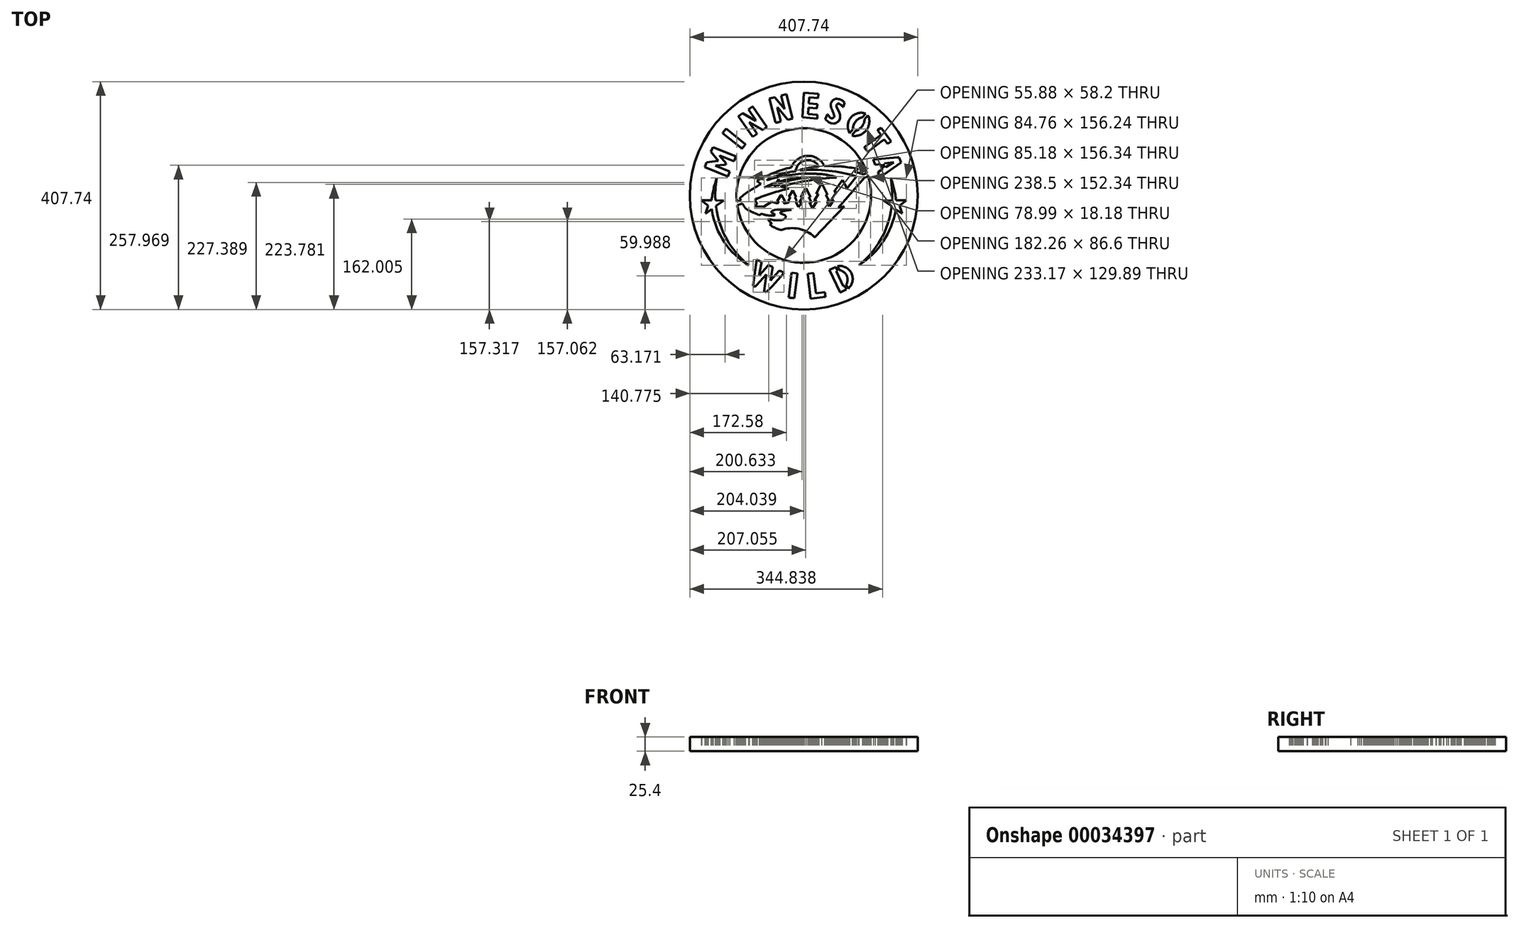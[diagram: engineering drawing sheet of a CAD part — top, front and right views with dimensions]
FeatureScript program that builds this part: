
annotation { "Feature Type Name" : "Feature", "Feature Type Description" : "" }
export const myFeature = defineFeature(function(context is Context, id is Id, definition is map)
    precondition{}
    {
        {
            var Q0;
            Q0=qCreatedBy(makeId("Top.planeOp"),FACE);
            var sketch = newSketch(context, id + "F0", { "sketchPlane" : qUnion([Q0])});
            skLineSegment(sketch, "E0", {"start": v(13.66, -184.3) * mm, "end": v(38.88, -181.07) * mm});
            skLineSegment(sketch, "E1", {"start": v(38.88, -181.07) * mm, "end": v(38.67, -180.35) * mm});
            skLineSegment(sketch, "E2", {"start": v(38.67, -180.35) * mm, "end": v(38.62, -180.14) * mm});
            skLineSegment(sketch, "E3", {"start": v(38.62, -180.14) * mm, "end": v(38.56, -179.8) * mm});
            skLineSegment(sketch, "E4", {"start": v(38.56, -179.8) * mm, "end": v(38.43, -178.87) * mm});
            skLineSegment(sketch, "E5", {"start": v(38.43, -178.87) * mm, "end": v(38.28, -177.67) * mm});
            skLineSegment(sketch, "E6", {"start": v(38.28, -177.67) * mm, "end": v(38.15, -176.34) * mm});
            skLineSegment(sketch, "E7", {"start": v(38.15, -176.34) * mm, "end": v(37.84, -173.04) * mm});
            skLineSegment(sketch, "E8", {"start": v(37.84, -173.04) * mm, "end": v(36.9, -173.04) * mm});
            skLineSegment(sketch, "E9", {"start": v(36.9, -173.04) * mm, "end": v(21.99, -174.94) * mm});
            skLineSegment(sketch, "E10", {"start": v(21.99, -174.94) * mm, "end": v(21.52, -174.47) * mm});
            skLineSegment(sketch, "E11", {"start": v(21.52, -174.47) * mm, "end": v(16.96, -139.2) * mm});
            skLineSegment(sketch, "E12", {"start": v(16.96, -139.2) * mm, "end": v(16.62, -138.84) * mm});
            skLineSegment(sketch, "E13", {"start": v(16.62, -138.84) * mm, "end": v(7.3, -139.96) * mm});
            skLineSegment(sketch, "E14", {"start": v(7.3, -139.96) * mm, "end": v(6.76, -140.57) * mm});
            skLineSegment(sketch, "E15", {"start": v(6.76, -140.57) * mm, "end": v(12.46, -184.17) * mm});
            skLineSegment(sketch, "E16", {"start": v(12.46, -184.17) * mm, "end": v(12.49, -184.28) * mm});
            skLineSegment(sketch, "E17", {"start": v(12.49, -184.28) * mm, "end": v(12.5, -184.3) * mm});
            skLineSegment(sketch, "E18", {"start": v(12.5, -184.3) * mm, "end": v(12.55, -184.32) * mm});
            skLineSegment(sketch, "E19", {"start": v(12.55, -184.32) * mm, "end": v(12.68, -184.35) * mm});
            skLineSegment(sketch, "E20", {"start": v(12.68, -184.35) * mm, "end": v(12.87, -184.36) * mm});
            skLineSegment(sketch, "E21", {"start": v(12.87, -184.36) * mm, "end": v(13.09, -184.34) * mm});
            skLineSegment(sketch, "E22", {"start": v(13.09, -184.34) * mm, "end": v(13.66, -184.3) * mm});
            skLineSegment(sketch, "E23", {"start": v(-16.77, -183.6) * mm, "end": v(-11.59, -139.7) * mm});
            skLineSegment(sketch, "E24", {"start": v(-11.59, -139.7) * mm, "end": v(-11.9, -139.4) * mm});
            skLineSegment(sketch, "E25", {"start": v(-11.9, -139.4) * mm, "end": v(-21.63, -138.21) * mm});
            skLineSegment(sketch, "E26", {"start": v(-21.63, -138.21) * mm, "end": v(-21.92, -139.2) * mm});
            skLineSegment(sketch, "E27", {"start": v(-21.92, -139.2) * mm, "end": v(-26.6, -179.63) * mm});
            skLineSegment(sketch, "E28", {"start": v(-26.6, -179.63) * mm, "end": v(-27.07, -182.45) * mm});
            skLineSegment(sketch, "E29", {"start": v(-27.07, -182.45) * mm, "end": v(-25.33, -182.72) * mm});
            skLineSegment(sketch, "E30", {"start": v(-25.33, -182.72) * mm, "end": v(-24.38, -182.85) * mm});
            skLineSegment(sketch, "E31", {"start": v(-24.38, -182.85) * mm, "end": v(-23.1, -183) * mm});
            skLineSegment(sketch, "E32", {"start": v(-23.1, -183) * mm, "end": v(-21.64, -183.16) * mm});
            skLineSegment(sketch, "E33", {"start": v(-21.64, -183.16) * mm, "end": v(-20.18, -183.3) * mm});
            skLineSegment(sketch, "E34", {"start": v(-20.18, -183.3) * mm, "end": v(-16.77, -183.6) * mm});
            skLineSegment(sketch, "E35", {"start": v(65, -173.44) * mm, "end": v(76.13, -168.01) * mm});
            skLineSegment(sketch, "E36", {"start": v(56.92, -127.66) * mm, "end": v(45.73, -133) * mm});
            skLineSegment(sketch, "E37", {"start": v(45.73, -133) * mm, "end": v(64.83, -173.27) * mm});
            skLineSegment(sketch, "E38", {"start": v(64.83, -173.27) * mm, "end": v(65, -173.44) * mm});
            skLineSegment(sketch, "E39", {"start": v(-67, -172.98) * mm, "end": v(-56.7, -161.92) * mm});
            skLineSegment(sketch, "E40", {"start": v(-56.7, -161.92) * mm, "end": v(-35.8, -139.2) * mm});
            skLineSegment(sketch, "E41", {"start": v(-35.8, -139.2) * mm, "end": v(-35.15, -138.14) * mm});
            skLineSegment(sketch, "E42", {"start": v(-35.15, -138.14) * mm, "end": v(-43.96, -133.96) * mm});
            skLineSegment(sketch, "E43", {"start": v(-43.96, -133.96) * mm, "end": v(-44.55, -134.67) * mm});
            skLineSegment(sketch, "E44", {"start": v(-44.55, -134.67) * mm, "end": v(-59.36, -152.18) * mm});
            skLineSegment(sketch, "E45", {"start": v(-59.36, -152.18) * mm, "end": v(-59.73, -151.81) * mm});
            skLineSegment(sketch, "E46", {"start": v(-59.73, -151.81) * mm, "end": v(-56.06, -128.63) * mm});
            skLineSegment(sketch, "E47", {"start": v(-56.06, -128.63) * mm, "end": v(-56.06, -128.06) * mm});
            skLineSegment(sketch, "E48", {"start": v(-56.06, -128.06) * mm, "end": v(-63.05, -124.87) * mm});
            skLineSegment(sketch, "E49", {"start": v(-63.05, -124.87) * mm, "end": v(-64, -125.24) * mm});
            skLineSegment(sketch, "E50", {"start": v(-64, -125.24) * mm, "end": v(-79.45, -142.55) * mm});
            skLineSegment(sketch, "E51", {"start": v(-79.45, -142.55) * mm, "end": v(-79.98, -142.61) * mm});
            skLineSegment(sketch, "E52", {"start": v(-79.98, -142.61) * mm, "end": v(-76.14, -121.95) * mm});
            skLineSegment(sketch, "E53", {"start": v(-76.14, -121.95) * mm, "end": v(-75.54, -118.77) * mm});
            skLineSegment(sketch, "E54", {"start": v(-75.54, -118.77) * mm, "end": v(-84.25, -114.78) * mm});
            skLineSegment(sketch, "E55", {"start": v(-84.25, -114.78) * mm, "end": v(-84.6, -115.14) * mm});
            skLineSegment(sketch, "E56", {"start": v(-84.6, -115.14) * mm, "end": v(-91.04, -160.1) * mm});
            skLineSegment(sketch, "E57", {"start": v(-91.04, -160.1) * mm, "end": v(-91.03, -161.67) * mm});
            skLineSegment(sketch, "E58", {"start": v(-91.03, -161.67) * mm, "end": v(-87.32, -163.57) * mm});
            skLineSegment(sketch, "E59", {"start": v(-87.32, -163.57) * mm, "end": v(-84.45, -160.3) * mm});
            skLineSegment(sketch, "E60", {"start": v(-84.45, -160.3) * mm, "end": v(-67.19, -141.39) * mm});
            skLineSegment(sketch, "E61", {"start": v(-67.19, -141.39) * mm, "end": v(-66.94, -142.84) * mm});
            skLineSegment(sketch, "E62", {"start": v(-66.94, -142.84) * mm, "end": v(-71, -170.98) * mm});
            skLineSegment(sketch, "E63", {"start": v(-71, -170.98) * mm, "end": v(-70.8, -171.17) * mm});
            skLineSegment(sketch, "E64", {"start": v(-70.8, -171.17) * mm, "end": v(-70.72, -171.23) * mm});
            skLineSegment(sketch, "E65", {"start": v(-70.72, -171.23) * mm, "end": v(-70.58, -171.31) * mm});
            skLineSegment(sketch, "E66", {"start": v(-70.58, -171.31) * mm, "end": v(-70.13, -171.55) * mm});
            skLineSegment(sketch, "E67", {"start": v(-70.13, -171.55) * mm, "end": v(-69.52, -171.85) * mm});
            skLineSegment(sketch, "E68", {"start": v(-69.52, -171.85) * mm, "end": v(-68.8, -172.18) * mm});
            skLineSegment(sketch, "E69", {"start": v(-68.8, -172.18) * mm, "end": v(-67, -172.98) * mm});
            skLineSegment(sketch, "E70", {"start": v(58.62, -136.07) * mm, "end": v(70.8, -162.14) * mm});
            skLineSegment(sketch, "E71", {"start": v(70.8, -162.14) * mm, "end": v(71, -162.14) * mm});
            skLineSegment(sketch, "E72", {"start": v(71, -162.14) * mm, "end": v(71.1, -162.12) * mm});
            skLineSegment(sketch, "E73", {"start": v(71.1, -162.12) * mm, "end": v(71.26, -162.05) * mm});
            skLineSegment(sketch, "E74", {"start": v(71.26, -162.05) * mm, "end": v(71.81, -161.78) * mm});
            skLineSegment(sketch, "E75", {"start": v(71.81, -161.78) * mm, "end": v(72.58, -161.4) * mm});
            skLineSegment(sketch, "E76", {"start": v(72.58, -161.4) * mm, "end": v(72.9, -161.22) * mm});
            skLineSegment(sketch, "E77", {"start": v(60.23, -134.6) * mm, "end": v(58.62, -135.24) * mm});
            skLineSegment(sketch, "E78", {"start": v(58.62, -135.24) * mm, "end": v(58.62, -136.07) * mm});
            skLineSegment(sketch, "E79", {"start": v(-157, -20.94) * mm, "end": v(-157.12, -18.94) * mm});
            skLineSegment(sketch, "E80", {"start": v(-157.12, -18.94) * mm, "end": v(-143.14, -8.86) * mm});
            skLineSegment(sketch, "E81", {"start": v(-143.14, -8.86) * mm, "end": v(-158.2, -8.6) * mm});
            skLineSegment(sketch, "E82", {"start": v(-165.07, -8.63) * mm, "end": v(-183.29, -8.63) * mm});
            skLineSegment(sketch, "E83", {"start": v(-183.29, -8.63) * mm, "end": v(-182.8, -9.43) * mm});
            skLineSegment(sketch, "E84", {"start": v(-182.8, -9.43) * mm, "end": v(-171.8, -17.37) * mm});
            skLineSegment(sketch, "E85", {"start": v(-171.8, -17.37) * mm, "end": v(-171.34, -18.6) * mm});
            skLineSegment(sketch, "E86", {"start": v(-171.34, -18.6) * mm, "end": v(-175.9, -32.25) * mm});
            skLineSegment(sketch, "E87", {"start": v(-175.9, -32.25) * mm, "end": v(-175.28, -32.2) * mm});
            skLineSegment(sketch, "E88", {"start": v(-175.28, -32.2) * mm, "end": v(-164.84, -24.62) * mm});
            skLineSegment(sketch, "E89", {"start": v(-164.84, -24.62) * mm, "end": v(-164.5, -24.83) * mm});
            skLineSegment(sketch, "E90", {"start": v(-164.5, -24.83) * mm, "end": v(-164.43, -24.89) * mm});
            skLineSegment(sketch, "E91", {"start": v(-164.43, -24.89) * mm, "end": v(-164.36, -24.99) * mm});
            skLineSegment(sketch, "E92", {"start": v(-164.36, -24.99) * mm, "end": v(-164.3, -25.11) * mm});
            skLineSegment(sketch, "E93", {"start": v(-164.3, -25.11) * mm, "end": v(-164.26, -25.26) * mm});
            skLineSegment(sketch, "E94", {"start": v(-164.26, -25.26) * mm, "end": v(-164.21, -25.44) * mm});
            skLineSegment(sketch, "E95", {"start": v(-164.21, -25.44) * mm, "end": v(-164.18, -25.63) * mm});
            skLineSegment(sketch, "E96", {"start": v(-164.18, -25.63) * mm, "end": v(-164.16, -25.82) * mm});
            skLineSegment(sketch, "E97", {"start": v(-164.16, -25.82) * mm, "end": v(-164.15, -26.03) * mm});
            skLineSegment(sketch, "E98", {"start": v(-164.15, -26.03) * mm, "end": v(-164.15, -27.02) * mm});
            skLineSegment(sketch, "E99", {"start": v(164.67, -24.98) * mm, "end": v(165.13, -24.98) * mm});
            skLineSegment(sketch, "E100", {"start": v(165.13, -24.98) * mm, "end": v(175.51, -32.25) * mm});
            skLineSegment(sketch, "E101", {"start": v(175.51, -32.25) * mm, "end": v(175.96, -32.25) * mm});
            skLineSegment(sketch, "E102", {"start": v(175.96, -32.25) * mm, "end": v(171.4, -18.6) * mm});
            skLineSegment(sketch, "E103", {"start": v(171.4, -18.6) * mm, "end": v(171.87, -17.37) * mm});
            skLineSegment(sketch, "E104", {"start": v(171.87, -17.37) * mm, "end": v(182.85, -9.43) * mm});
            skLineSegment(sketch, "E105", {"start": v(182.85, -9.43) * mm, "end": v(183.35, -8.63) * mm});
            skLineSegment(sketch, "E106", {"start": v(183.35, -8.63) * mm, "end": v(165.17, -8.63) * mm});
            skLineSegment(sketch, "E107", {"start": v(158.25, -8.6) * mm, "end": v(143.2, -8.86) * mm});
            skLineSegment(sketch, "E108", {"start": v(143.2, -8.86) * mm, "end": v(157.18, -18.94) * mm});
            skLineSegment(sketch, "E109", {"start": v(157.18, -18.94) * mm, "end": v(157.06, -20.94) * mm});
            skLineSegment(sketch, "E110", {"start": v(19.39, -74.33) * mm, "end": v(19.67, -74.26) * mm});
            skLineSegment(sketch, "E111", {"start": v(19.67, -74.26) * mm, "end": v(72.6, -19.3) * mm});
            skLineSegment(sketch, "E112", {"start": v(72.6, -19.3) * mm, "end": v(61.4, -21.73) * mm});
            skLineSegment(sketch, "E113", {"start": v(61.4, -21.73) * mm, "end": v(108.8, 32.15) * mm});
            skLineSegment(sketch, "E114", {"start": v(90.99, 42.52) * mm, "end": v(97.42, 47.42) * mm});
            skLineSegment(sketch, "E115", {"start": v(97.42, 47.42) * mm, "end": v(97.18, 47.66) * mm});
            skLineSegment(sketch, "E116", {"start": v(-83.9, 25.97) * mm, "end": v(-76.46, 20.53) * mm});
            skLineSegment(sketch, "E117", {"start": v(-100.7, -25.36) * mm, "end": v(-95.75, -27.84) * mm});
            skLineSegment(sketch, "E118", {"start": v(-82.13, -34) * mm, "end": v(-79.8, -34.9) * mm});
            skLineSegment(sketch, "E119", {"start": v(-79.8, -34.9) * mm, "end": v(-75.2, -32.78) * mm});
            skLineSegment(sketch, "E120", {"start": v(-75.2, -32.78) * mm, "end": v(-71.8, -33.86) * mm});
            skLineSegment(sketch, "E121", {"start": v(-65.51, -35.4) * mm, "end": v(-62.65, -35.87) * mm});
            skLineSegment(sketch, "E122", {"start": v(-62.65, -35.87) * mm, "end": v(-53.83, -35.88) * mm});
            skLineSegment(sketch, "E123", {"start": v(-53.83, -35.88) * mm, "end": v(-51.5, -34.82) * mm});
            skLineSegment(sketch, "E124", {"start": v(-51.5, -34.82) * mm, "end": v(-51.65, -34.33) * mm});
            skLineSegment(sketch, "E125", {"start": v(-54.73, -32.24) * mm, "end": v(-57.64, -30.65) * mm});
            skLineSegment(sketch, "E126", {"start": v(-56.42, -27.3) * mm, "end": v(-52.2, -25.85) * mm});
            skLineSegment(sketch, "E127", {"start": v(-52.2, -25.85) * mm, "end": v(-42.04, -24.87) * mm});
            skLineSegment(sketch, "E128", {"start": v(-42.04, -24.87) * mm, "end": v(-22.22, -25.6) * mm});
            skLineSegment(sketch, "E129", {"start": v(-38.74, -28.2) * mm, "end": v(-41.75, -30.24) * mm});
            skLineSegment(sketch, "E130", {"start": v(-41.75, -30.24) * mm, "end": v(-41.75, -31.97) * mm});
            skLineSegment(sketch, "E131", {"start": v(-41.75, -31.97) * mm, "end": v(-33.72, -35.39) * mm});
            skLineSegment(sketch, "E132", {"start": v(-32.44, -38.94) * mm, "end": v(-34.35, -41.36) * mm});
            skLineSegment(sketch, "E133", {"start": v(-43.12, -44.24) * mm, "end": v(-53.56, -44.28) * mm});
            skLineSegment(sketch, "E134", {"start": v(-53.56, -44.28) * mm, "end": v(-62.37, -42.12) * mm});
            skLineSegment(sketch, "E135", {"start": v(-62.37, -42.12) * mm, "end": v(-63.81, -42.68) * mm});
            skLineSegment(sketch, "E136", {"start": v(-63.81, -42.68) * mm, "end": v(-62.45, -45.31) * mm});
            skLineSegment(sketch, "E137", {"start": v(-62.45, -45.31) * mm, "end": v(-60.33, -47.18) * mm});
            skLineSegment(sketch, "E138", {"start": v(-57.79, -49.05) * mm, "end": v(-57.37, -49.05) * mm});
            skLineSegment(sketch, "E139", {"start": v(-57.37, -49.05) * mm, "end": v(-57.65, -49.5) * mm});
            skLineSegment(sketch, "E140", {"start": v(-59.53, -50.79) * mm, "end": v(-61.13, -51.6) * mm});
            skLineSegment(sketch, "E141", {"start": v(-61.13, -51.6) * mm, "end": v(-57.28, -55.08) * mm});
            skLineSegment(sketch, "E142", {"start": v(23.78, -9.76) * mm, "end": v(19.33, -9.49) * mm});
            skLineSegment(sketch, "E143", {"start": v(19.33, -9.49) * mm, "end": v(19.33, -8.67) * mm});
            skLineSegment(sketch, "E144", {"start": v(19.33, -8.67) * mm, "end": v(25.8, 1.58) * mm});
            skLineSegment(sketch, "E145", {"start": v(25.8, 1.58) * mm, "end": v(26.24, 2.73) * mm});
            skLineSegment(sketch, "E146", {"start": v(26.24, 2.73) * mm, "end": v(24.15, 2.73) * mm});
            skLineSegment(sketch, "E147", {"start": v(24.15, 2.73) * mm, "end": v(23.34, 2.74) * mm});
            skLineSegment(sketch, "E148", {"start": v(23.34, 2.74) * mm, "end": v(22.67, 2.78) * mm});
            skLineSegment(sketch, "E149", {"start": v(22.67, 2.78) * mm, "end": v(22.42, 2.8) * mm});
            skLineSegment(sketch, "E150", {"start": v(22.42, 2.8) * mm, "end": v(22.22, 2.83) * mm});
            skLineSegment(sketch, "E151", {"start": v(22.22, 2.83) * mm, "end": v(22.1, 2.86) * mm});
            skLineSegment(sketch, "E152", {"start": v(22.1, 2.86) * mm, "end": v(22.07, 2.88) * mm});
            skLineSegment(sketch, "E153", {"start": v(22.07, 2.88) * mm, "end": v(22.06, 2.9) * mm});
            skLineSegment(sketch, "E154", {"start": v(22.06, 2.9) * mm, "end": v(22.06, 3.06) * mm});
            skLineSegment(sketch, "E155", {"start": v(22.06, 3.06) * mm, "end": v(32.04, 22.88) * mm});
            skLineSegment(sketch, "E156", {"start": v(32.04, 22.88) * mm, "end": v(42.04, 2.22) * mm});
            skLineSegment(sketch, "E157", {"start": v(42.04, 2.22) * mm, "end": v(42.04, 1.42) * mm});
            skLineSegment(sketch, "E158", {"start": v(42.04, 1.42) * mm, "end": v(39.3, 1.14) * mm});
            skLineSegment(sketch, "E159", {"start": v(39.3, 1.14) * mm, "end": v(45.22, -9.08) * mm});
            skLineSegment(sketch, "E160", {"start": v(45.22, -9.08) * mm, "end": v(45.22, -9.3) * mm});
            skLineSegment(sketch, "E161", {"start": v(45.22, -9.3) * mm, "end": v(45.21, -9.33) * mm});
            skLineSegment(sketch, "E162", {"start": v(45.21, -9.33) * mm, "end": v(45.18, -9.35) * mm});
            skLineSegment(sketch, "E163", {"start": v(45.18, -9.35) * mm, "end": v(45.06, -9.4) * mm});
            skLineSegment(sketch, "E164", {"start": v(45.06, -9.4) * mm, "end": v(44.87, -9.44) * mm});
            skLineSegment(sketch, "E165", {"start": v(44.87, -9.44) * mm, "end": v(44.62, -9.47) * mm});
            skLineSegment(sketch, "E166", {"start": v(44.62, -9.47) * mm, "end": v(44.32, -9.5) * mm});
            skLineSegment(sketch, "E167", {"start": v(44.32, -9.5) * mm, "end": v(43.97, -9.52) * mm});
            skLineSegment(sketch, "E168", {"start": v(43.97, -9.52) * mm, "end": v(43.58, -9.53) * mm});
            skLineSegment(sketch, "E169", {"start": v(43.58, -9.53) * mm, "end": v(43.17, -9.54) * mm});
            skLineSegment(sketch, "E170", {"start": v(43.17, -9.54) * mm, "end": v(41.12, -9.54) * mm});
            skLineSegment(sketch, "E171", {"start": v(41.12, -9.54) * mm, "end": v(41.76, -11.01) * mm});
            skLineSegment(sketch, "E172", {"start": v(41.76, -11.01) * mm, "end": v(42.14, -11.87) * mm});
            skLineSegment(sketch, "E173", {"start": v(42.14, -11.87) * mm, "end": v(42.7, -13.1) * mm});
            skLineSegment(sketch, "E174", {"start": v(42.7, -13.1) * mm, "end": v(44.08, -16.05) * mm});
            skLineSegment(sketch, "E175", {"start": v(44.08, -16.05) * mm, "end": v(45.77, -19.62) * mm});
            skLineSegment(sketch, "E176", {"start": v(45.77, -19.62) * mm, "end": v(46.45, -18.85) * mm});
            skLineSegment(sketch, "E177", {"start": v(46.45, -18.85) * mm, "end": v(53.4, -8.15) * mm});
            skLineSegment(sketch, "E178", {"start": v(53.4, -8.15) * mm, "end": v(53.4, -7.94) * mm});
            skLineSegment(sketch, "E179", {"start": v(53.4, -7.94) * mm, "end": v(53.39, -7.91) * mm});
            skLineSegment(sketch, "E180", {"start": v(53.39, -7.91) * mm, "end": v(53.36, -7.9) * mm});
            skLineSegment(sketch, "E181", {"start": v(53.36, -7.9) * mm, "end": v(53.25, -7.85) * mm});
            skLineSegment(sketch, "E182", {"start": v(53.25, -7.85) * mm, "end": v(53.09, -7.82) * mm});
            skLineSegment(sketch, "E183", {"start": v(53.09, -7.82) * mm, "end": v(52.86, -7.78) * mm});
            skLineSegment(sketch, "E184", {"start": v(52.86, -7.78) * mm, "end": v(52.6, -7.76) * mm});
            skLineSegment(sketch, "E185", {"start": v(52.6, -7.76) * mm, "end": v(52.29, -7.74) * mm});
            skLineSegment(sketch, "E186", {"start": v(52.29, -7.74) * mm, "end": v(51.95, -7.73) * mm});
            skLineSegment(sketch, "E187", {"start": v(51.95, -7.73) * mm, "end": v(51.58, -7.72) * mm});
            skLineSegment(sketch, "E188", {"start": v(51.58, -7.72) * mm, "end": v(49.76, -7.72) * mm});
            skLineSegment(sketch, "E189", {"start": v(49.76, -7.72) * mm, "end": v(49.8, -6.59) * mm});
            skLineSegment(sketch, "E190", {"start": v(49.8, -6.59) * mm, "end": v(58.78, 6.13) * mm});
            skLineSegment(sketch, "E191", {"start": v(58.78, 6.13) * mm, "end": v(53.93, 6.59) * mm});
            skLineSegment(sketch, "E192", {"start": v(53.93, 6.59) * mm, "end": v(68.7, 26.85) * mm});
            skLineSegment(sketch, "E193", {"start": v(68.7, 26.85) * mm, "end": v(69.52, 27.66) * mm});
            skLineSegment(sketch, "E194", {"start": v(69.52, 27.66) * mm, "end": v(77.24, 13.66) * mm});
            skLineSegment(sketch, "E195", {"start": v(77.24, 13.66) * mm, "end": v(77.9, 13.85) * mm});
            skLineSegment(sketch, "E196", {"start": v(77.9, 13.85) * mm, "end": v(94.31, 33.98) * mm});
            skLineSegment(sketch, "E197", {"start": v(-6.31, 45.08) * mm, "end": v(-6.24, 46.2) * mm});
            skLineSegment(sketch, "E198", {"start": v(-64.64, 28.57) * mm, "end": v(-65, 28.42) * mm});
            skLineSegment(sketch, "E199", {"start": v(-65, 28.42) * mm, "end": v(-65.28, 28.29) * mm});
            skLineSegment(sketch, "E200", {"start": v(-65.28, 28.29) * mm, "end": v(-65.48, 28.18) * mm});
            skLineSegment(sketch, "E201", {"start": v(-65.48, 28.18) * mm, "end": v(-65.6, 28.1) * mm});
            skLineSegment(sketch, "E202", {"start": v(-65.6, 28.1) * mm, "end": v(-65.64, 28.06) * mm});
            skLineSegment(sketch, "E203", {"start": v(-65.64, 28.06) * mm, "end": v(-65.65, 28.02) * mm});
            skLineSegment(sketch, "E204", {"start": v(-65.65, 28.02) * mm, "end": v(-65.65, 28) * mm});
            skLineSegment(sketch, "E205", {"start": v(-65.65, 28) * mm, "end": v(-65.63, 27.98) * mm});
            skLineSegment(sketch, "E206", {"start": v(-65.63, 27.98) * mm, "end": v(-65.6, 27.96) * mm});
            skLineSegment(sketch, "E207", {"start": v(-65.6, 27.96) * mm, "end": v(-65.55, 27.95) * mm});
            skLineSegment(sketch, "E208", {"start": v(-65.55, 27.95) * mm, "end": v(-65.4, 27.95) * mm});
            skLineSegment(sketch, "E209", {"start": v(-65.4, 27.95) * mm, "end": v(-65.2, 27.96) * mm});
            skLineSegment(sketch, "E210", {"start": v(-65.2, 27.96) * mm, "end": v(-64.93, 28) * mm});
            skLineSegment(sketch, "E211", {"start": v(-64.93, 28) * mm, "end": v(-64.62, 28.06) * mm});
            skLineSegment(sketch, "E212", {"start": v(-64.62, 28.06) * mm, "end": v(-64.26, 28.13) * mm});
            skLineSegment(sketch, "E213", {"start": v(-64.26, 28.13) * mm, "end": v(-63.85, 28.23) * mm});
            skLineSegment(sketch, "E214", {"start": v(-63.85, 28.23) * mm, "end": v(-63.4, 28.35) * mm});
            skLineSegment(sketch, "E215", {"start": v(-63.4, 28.35) * mm, "end": v(-62.92, 28.48) * mm});
            skLineSegment(sketch, "E216", {"start": v(22.39, 39.08) * mm, "end": v(23.65, 38.66) * mm});
            skLineSegment(sketch, "E217", {"start": v(-87.17, -6.94) * mm, "end": v(-87.94, -7.63) * mm});
            skLineSegment(sketch, "E218", {"start": v(-87.94, -7.63) * mm, "end": v(-83.77, -13.73) * mm});
            skLineSegment(sketch, "E219", {"start": v(-83.77, -13.73) * mm, "end": v(-83.77, -14.18) * mm});
            skLineSegment(sketch, "E220", {"start": v(-83.77, -14.18) * mm, "end": v(-83.78, -14.24) * mm});
            skLineSegment(sketch, "E221", {"start": v(-83.78, -14.24) * mm, "end": v(-83.8, -14.32) * mm});
            skLineSegment(sketch, "E222", {"start": v(-83.8, -14.32) * mm, "end": v(-83.9, -14.53) * mm});
            skLineSegment(sketch, "E223", {"start": v(-83.9, -14.53) * mm, "end": v(-84.08, -14.8) * mm});
            skLineSegment(sketch, "E224", {"start": v(-84.08, -14.8) * mm, "end": v(-84.3, -15.14) * mm});
            skLineSegment(sketch, "E225", {"start": v(-84.3, -15.14) * mm, "end": v(-84.57, -15.52) * mm});
            skLineSegment(sketch, "E226", {"start": v(-84.57, -15.52) * mm, "end": v(-84.88, -15.93) * mm});
            skLineSegment(sketch, "E227", {"start": v(-84.88, -15.93) * mm, "end": v(-85.22, -16.36) * mm});
            skLineSegment(sketch, "E228", {"start": v(-85.22, -16.36) * mm, "end": v(-85.58, -16.8) * mm});
            skLineSegment(sketch, "E229", {"start": v(-85.58, -16.8) * mm, "end": v(-87.4, -18.98) * mm});
            skLineSegment(sketch, "E230", {"start": v(-87.4, -18.98) * mm, "end": v(-85.81, -19.62) * mm});
            skLineSegment(sketch, "E231", {"start": v(-85.81, -19.62) * mm, "end": v(-71.99, -20.11) * mm});
            skLineSegment(sketch, "E232", {"start": v(-71.99, -20.11) * mm, "end": v(-57.91, -11.28) * mm});
            skLineSegment(sketch, "E233", {"start": v(-57.91, -11.28) * mm, "end": v(-46.97, -14.42) * mm});
            skLineSegment(sketch, "E234", {"start": v(-46.97, -14.42) * mm, "end": v(-44.2, -10.67) * mm});
            skLineSegment(sketch, "E235", {"start": v(-44.2, -10.67) * mm, "end": v(-45.82, -10.53) * mm});
            skLineSegment(sketch, "E236", {"start": v(-45.82, -10.53) * mm, "end": v(-46.14, -10.5) * mm});
            skLineSegment(sketch, "E237", {"start": v(-46.14, -10.5) * mm, "end": v(-46.45, -10.46) * mm});
            skLineSegment(sketch, "E238", {"start": v(-46.45, -10.46) * mm, "end": v(-46.72, -10.42) * mm});
            skLineSegment(sketch, "E239", {"start": v(-46.72, -10.42) * mm, "end": v(-46.96, -10.37) * mm});
            skLineSegment(sketch, "E240", {"start": v(-46.96, -10.37) * mm, "end": v(-47.16, -10.32) * mm});
            skLineSegment(sketch, "E241", {"start": v(-47.16, -10.32) * mm, "end": v(-47.3, -10.27) * mm});
            skLineSegment(sketch, "E242", {"start": v(-47.3, -10.27) * mm, "end": v(-47.4, -10.22) * mm});
            skLineSegment(sketch, "E243", {"start": v(-47.4, -10.22) * mm, "end": v(-47.42, -10.2) * mm});
            skLineSegment(sketch, "E244", {"start": v(-47.42, -10.2) * mm, "end": v(-47.43, -10.17) * mm});
            skLineSegment(sketch, "E245", {"start": v(-47.43, -10.17) * mm, "end": v(-47.43, -9.95) * mm});
            skLineSegment(sketch, "E246", {"start": v(-47.43, -9.95) * mm, "end": v(-40.55, 0.9) * mm});
            skLineSegment(sketch, "E247", {"start": v(-40.55, 0.9) * mm, "end": v(-39.94, 0.9) * mm});
            skLineSegment(sketch, "E248", {"start": v(-39.94, 0.9) * mm, "end": v(-34.49, -9.31) * mm});
            skLineSegment(sketch, "E249", {"start": v(-34.49, -9.31) * mm, "end": v(-34.2, -10.45) * mm});
            skLineSegment(sketch, "E250", {"start": v(-34.2, -10.45) * mm, "end": v(-35.36, -10.45) * mm});
            skLineSegment(sketch, "E251", {"start": v(-35.36, -10.45) * mm, "end": v(-35.81, -10.45) * mm});
            skLineSegment(sketch, "E252", {"start": v(-35.81, -10.45) * mm, "end": v(-36, -10.45) * mm});
            skLineSegment(sketch, "E253", {"start": v(-36, -10.45) * mm, "end": v(-36.14, -10.46) * mm});
            skLineSegment(sketch, "E254", {"start": v(-36.14, -10.46) * mm, "end": v(-36.26, -10.49) * mm});
            skLineSegment(sketch, "E255", {"start": v(-36.26, -10.49) * mm, "end": v(-36.35, -10.53) * mm});
            skLineSegment(sketch, "E256", {"start": v(-36.35, -10.53) * mm, "end": v(-36.41, -10.58) * mm});
            skLineSegment(sketch, "E257", {"start": v(-36.41, -10.58) * mm, "end": v(-36.45, -10.66) * mm});
            skLineSegment(sketch, "E258", {"start": v(-36.45, -10.66) * mm, "end": v(-36.45, -10.76) * mm});
            skLineSegment(sketch, "E259", {"start": v(-36.45, -10.76) * mm, "end": v(-36.44, -10.9) * mm});
            skLineSegment(sketch, "E260", {"start": v(-36.44, -10.9) * mm, "end": v(-36.4, -11.06) * mm});
            skLineSegment(sketch, "E261", {"start": v(-36.4, -11.06) * mm, "end": v(-36.33, -11.25) * mm});
            skLineSegment(sketch, "E262", {"start": v(-36.33, -11.25) * mm, "end": v(-36.12, -11.77) * mm});
            skLineSegment(sketch, "E263", {"start": v(-36.12, -11.77) * mm, "end": v(-35.83, -12.46) * mm});
            skLineSegment(sketch, "E264", {"start": v(-35.83, -12.46) * mm, "end": v(-35.14, -14.13) * mm});
            skLineSegment(sketch, "E265", {"start": v(-35.14, -14.13) * mm, "end": v(-34.36, -13.92) * mm});
            skLineSegment(sketch, "E266", {"start": v(-34.36, -13.92) * mm, "end": v(-33.82, -13.8) * mm});
            skLineSegment(sketch, "E267", {"start": v(-33.82, -13.8) * mm, "end": v(-32.94, -13.61) * mm});
            skLineSegment(sketch, "E268", {"start": v(-32.94, -13.61) * mm, "end": v(-31.83, -13.4) * mm});
            skLineSegment(sketch, "E269", {"start": v(-31.83, -13.4) * mm, "end": v(-30.63, -13.18) * mm});
            skLineSegment(sketch, "E270", {"start": v(-30.63, -13.18) * mm, "end": v(-27.67, -12.65) * mm});
            skLineSegment(sketch, "E271", {"start": v(-27.67, -12.65) * mm, "end": v(-25.12, -9.08) * mm});
            skLineSegment(sketch, "E272", {"start": v(-25.12, -9.08) * mm, "end": v(-26.28, -9.08) * mm});
            skLineSegment(sketch, "E273", {"start": v(-26.28, -9.08) * mm, "end": v(-26.52, -9.08) * mm});
            skLineSegment(sketch, "E274", {"start": v(-26.52, -9.08) * mm, "end": v(-26.73, -9.07) * mm});
            skLineSegment(sketch, "E275", {"start": v(-26.73, -9.07) * mm, "end": v(-26.93, -9.05) * mm});
            skLineSegment(sketch, "E276", {"start": v(-26.93, -9.05) * mm, "end": v(-27.1, -9.02) * mm});
            skLineSegment(sketch, "E277", {"start": v(-27.1, -9.02) * mm, "end": v(-27.25, -8.99) * mm});
            skLineSegment(sketch, "E278", {"start": v(-27.25, -8.99) * mm, "end": v(-27.36, -8.95) * mm});
            skLineSegment(sketch, "E279", {"start": v(-27.36, -8.95) * mm, "end": v(-27.42, -8.9) * mm});
            skLineSegment(sketch, "E280", {"start": v(-27.42, -8.9) * mm, "end": v(-27.44, -8.89) * mm});
            skLineSegment(sketch, "E281", {"start": v(-27.44, -8.89) * mm, "end": v(-27.45, -8.86) * mm});
            skLineSegment(sketch, "E282", {"start": v(-27.45, -8.86) * mm, "end": v(-27.45, -8.65) * mm});
            skLineSegment(sketch, "E283", {"start": v(-27.45, -8.65) * mm, "end": v(-23.82, -2.72) * mm});
            skLineSegment(sketch, "E284", {"start": v(-23.82, -2.72) * mm, "end": v(-24.88, -2.72) * mm});
            skLineSegment(sketch, "E285", {"start": v(-24.88, -2.72) * mm, "end": v(-25.1, -2.72) * mm});
            skLineSegment(sketch, "E286", {"start": v(-25.1, -2.72) * mm, "end": v(-25.3, -2.7) * mm});
            skLineSegment(sketch, "E287", {"start": v(-25.3, -2.7) * mm, "end": v(-25.51, -2.68) * mm});
            skLineSegment(sketch, "E288", {"start": v(-25.51, -2.68) * mm, "end": v(-25.7, -2.65) * mm});
            skLineSegment(sketch, "E289", {"start": v(-25.7, -2.65) * mm, "end": v(-25.86, -2.61) * mm});
            skLineSegment(sketch, "E290", {"start": v(-25.86, -2.61) * mm, "end": v(-26, -2.57) * mm});
            skLineSegment(sketch, "E291", {"start": v(-26, -2.57) * mm, "end": v(-26.11, -2.52) * mm});
            skLineSegment(sketch, "E292", {"start": v(-26.11, -2.52) * mm, "end": v(-26.18, -2.47) * mm});
            skLineSegment(sketch, "E293", {"start": v(-26.18, -2.47) * mm, "end": v(-26.44, -2.22) * mm});
            skLineSegment(sketch, "E294", {"start": v(-19.58, 9.3) * mm, "end": v(-13.97, -2.5) * mm});
            skLineSegment(sketch, "E295", {"start": v(-13.97, -2.5) * mm, "end": v(-16.15, -2.8) * mm});
            skLineSegment(sketch, "E296", {"start": v(-16.15, -2.8) * mm, "end": v(-16, -3.1) * mm});
            skLineSegment(sketch, "E297", {"start": v(-16, -3.1) * mm, "end": v(-15.47, -4.15) * mm});
            skLineSegment(sketch, "E298", {"start": v(-15.47, -4.15) * mm, "end": v(-14.39, -6.23) * mm});
            skLineSegment(sketch, "E299", {"start": v(-14.39, -6.23) * mm, "end": v(-14.1, -6.8) * mm});
            skLineSegment(sketch, "E300", {"start": v(-14.1, -6.8) * mm, "end": v(-13.81, -7.37) * mm});
            skLineSegment(sketch, "E301", {"start": v(-13.81, -7.37) * mm, "end": v(-13.56, -7.9) * mm});
            skLineSegment(sketch, "E302", {"start": v(-13.56, -7.9) * mm, "end": v(-13.35, -8.37) * mm});
            skLineSegment(sketch, "E303", {"start": v(-13.35, -8.37) * mm, "end": v(-13.17, -8.79) * mm});
            skLineSegment(sketch, "E304", {"start": v(-13.17, -8.79) * mm, "end": v(-13.03, -9.13) * mm});
            skLineSegment(sketch, "E305", {"start": v(-13.03, -9.13) * mm, "end": v(-12.94, -9.39) * mm});
            skLineSegment(sketch, "E306", {"start": v(-12.94, -9.39) * mm, "end": v(-12.92, -9.48) * mm});
            skLineSegment(sketch, "E307", {"start": v(-12.92, -9.48) * mm, "end": v(-12.91, -9.54) * mm});
            skLineSegment(sketch, "E308", {"start": v(-12.91, -9.54) * mm, "end": v(-12.91, -10.03) * mm});
            skLineSegment(sketch, "E309", {"start": v(-12.91, -10.03) * mm, "end": v(-13.48, -9.96) * mm});
            skLineSegment(sketch, "E310", {"start": v(-13.48, -9.96) * mm, "end": v(-13.75, -9.93) * mm});
            skLineSegment(sketch, "E311", {"start": v(-13.75, -9.93) * mm, "end": v(-14.06, -9.92) * mm});
            skLineSegment(sketch, "E312", {"start": v(-14.06, -9.92) * mm, "end": v(-14.38, -9.92) * mm});
            skLineSegment(sketch, "E313", {"start": v(-14.38, -9.92) * mm, "end": v(-14.66, -9.94) * mm});
            skLineSegment(sketch, "E314", {"start": v(-14.66, -9.94) * mm, "end": v(-15.26, -10) * mm});
            skLineSegment(sketch, "E315", {"start": v(-9.6, -20.5) * mm, "end": v(-8.96, -19.76) * mm});
            skLineSegment(sketch, "E316", {"start": v(-8.96, -19.76) * mm, "end": v(-3.83, -12.73) * mm});
            skLineSegment(sketch, "E317", {"start": v(-3.83, -12.73) * mm, "end": v(-3.83, -12.5) * mm});
            skLineSegment(sketch, "E318", {"start": v(-3.83, -12.5) * mm, "end": v(-3.84, -12.47) * mm});
            skLineSegment(sketch, "E319", {"start": v(-3.84, -12.47) * mm, "end": v(-3.87, -12.45) * mm});
            skLineSegment(sketch, "E320", {"start": v(-3.87, -12.45) * mm, "end": v(-3.97, -12.4) * mm});
            skLineSegment(sketch, "E321", {"start": v(-3.97, -12.4) * mm, "end": v(-4.14, -12.36) * mm});
            skLineSegment(sketch, "E322", {"start": v(-4.14, -12.36) * mm, "end": v(-4.36, -12.33) * mm});
            skLineSegment(sketch, "E323", {"start": v(-4.36, -12.33) * mm, "end": v(-4.63, -12.3) * mm});
            skLineSegment(sketch, "E324", {"start": v(-4.63, -12.3) * mm, "end": v(-4.94, -12.28) * mm});
            skLineSegment(sketch, "E325", {"start": v(-4.94, -12.28) * mm, "end": v(-5.28, -12.27) * mm});
            skLineSegment(sketch, "E326", {"start": v(-5.28, -12.27) * mm, "end": v(-5.65, -12.26) * mm});
            skLineSegment(sketch, "E327", {"start": v(-5.65, -12.26) * mm, "end": v(-6.01, -12.26) * mm});
            skLineSegment(sketch, "E328", {"start": v(-6.01, -12.26) * mm, "end": v(-6.35, -12.24) * mm});
            skLineSegment(sketch, "E329", {"start": v(-6.35, -12.24) * mm, "end": v(-6.66, -12.22) * mm});
            skLineSegment(sketch, "E330", {"start": v(-6.66, -12.22) * mm, "end": v(-6.93, -12.2) * mm});
            skLineSegment(sketch, "E331", {"start": v(-6.93, -12.2) * mm, "end": v(-7.15, -12.16) * mm});
            skLineSegment(sketch, "E332", {"start": v(-7.15, -12.16) * mm, "end": v(-7.32, -12.12) * mm});
            skLineSegment(sketch, "E333", {"start": v(-7.32, -12.12) * mm, "end": v(-7.43, -12.07) * mm});
            skLineSegment(sketch, "E334", {"start": v(-7.43, -12.07) * mm, "end": v(-7.45, -12.05) * mm});
            skLineSegment(sketch, "E335", {"start": v(-7.45, -12.05) * mm, "end": v(-7.46, -12.02) * mm});
            skLineSegment(sketch, "E336", {"start": v(-7.46, -12.02) * mm, "end": v(-7.46, -11.78) * mm});
            skLineSegment(sketch, "E337", {"start": v(-7.46, -11.78) * mm, "end": v(-1.59, -2.72) * mm});
            skLineSegment(sketch, "E338", {"start": v(-1.59, -2.72) * mm, "end": v(-5.2, -2.72) * mm});
            skLineSegment(sketch, "E339", {"start": v(-5.2, -2.72) * mm, "end": v(-5.19, -2.04) * mm});
            skLineSegment(sketch, "E340", {"start": v(-5.19, -2.04) * mm, "end": v(-3.03, 1.66) * mm});
            skLineSegment(sketch, "E341", {"start": v(-3.03, 1.66) * mm, "end": v(1.4, 9.26) * mm});
            skLineSegment(sketch, "E342", {"start": v(1.4, 9.26) * mm, "end": v(3.66, 13.17) * mm});
            skLineSegment(sketch, "E343", {"start": v(3.66, 13.17) * mm, "end": v(4.13, 13.17) * mm});
            skLineSegment(sketch, "E344", {"start": v(4.13, 13.17) * mm, "end": v(12.06, -2.72) * mm});
            skLineSegment(sketch, "E345", {"start": v(12.06, -2.72) * mm, "end": v(8.87, -2.72) * mm});
            skLineSegment(sketch, "E346", {"start": v(8.87, -2.72) * mm, "end": v(9.84, -4.65) * mm});
            skLineSegment(sketch, "E347", {"start": v(9.84, -4.65) * mm, "end": v(10.34, -5.6) * mm});
            skLineSegment(sketch, "E348", {"start": v(10.34, -5.6) * mm, "end": v(10.98, -6.77) * mm});
            skLineSegment(sketch, "E349", {"start": v(10.98, -6.77) * mm, "end": v(11.67, -8) * mm});
            skLineSegment(sketch, "E350", {"start": v(11.67, -8) * mm, "end": v(12.35, -9.14) * mm});
            skLineSegment(sketch, "E351", {"start": v(12.35, -9.14) * mm, "end": v(12.94, -10.16) * mm});
            skLineSegment(sketch, "E352", {"start": v(12.94, -10.16) * mm, "end": v(13.43, -11.02) * mm});
            skLineSegment(sketch, "E353", {"start": v(13.43, -11.02) * mm, "end": v(13.76, -11.65) * mm});
            skLineSegment(sketch, "E354", {"start": v(13.76, -11.65) * mm, "end": v(13.85, -11.85) * mm});
            skLineSegment(sketch, "E355", {"start": v(13.85, -11.85) * mm, "end": v(13.88, -11.96) * mm});
            skLineSegment(sketch, "E356", {"start": v(13.88, -11.96) * mm, "end": v(13.87, -11.98) * mm});
            skLineSegment(sketch, "E357", {"start": v(13.87, -11.98) * mm, "end": v(13.85, -12) * mm});
            skLineSegment(sketch, "E358", {"start": v(13.85, -12) * mm, "end": v(13.74, -12.07) * mm});
            skLineSegment(sketch, "E359", {"start": v(13.74, -12.07) * mm, "end": v(13.58, -12.12) * mm});
            skLineSegment(sketch, "E360", {"start": v(13.58, -12.12) * mm, "end": v(13.36, -12.18) * mm});
            skLineSegment(sketch, "E361", {"start": v(13.36, -12.18) * mm, "end": v(13.1, -12.23) * mm});
            skLineSegment(sketch, "E362", {"start": v(13.1, -12.23) * mm, "end": v(12.8, -12.28) * mm});
            skLineSegment(sketch, "E363", {"start": v(12.8, -12.28) * mm, "end": v(12.47, -12.32) * mm});
            skLineSegment(sketch, "E364", {"start": v(12.47, -12.32) * mm, "end": v(12.11, -12.35) * mm});
            skLineSegment(sketch, "E365", {"start": v(12.11, -12.35) * mm, "end": v(10.34, -12.49) * mm});
            skLineSegment(sketch, "E366", {"start": v(10.34, -12.49) * mm, "end": v(15.53, -23.39) * mm});
            skLineSegment(sketch, "E367", {"start": v(-70.79, 14.43) * mm, "end": v(-50.38, 20.81) * mm});
            skLineSegment(sketch, "E368", {"start": v(-50.38, 20.81) * mm, "end": v(-50.25, 20.68) * mm});
            skLineSegment(sketch, "E369", {"start": v(-50.25, 20.68) * mm, "end": v(-50.24, 20.66) * mm});
            skLineSegment(sketch, "E370", {"start": v(-50.24, 20.66) * mm, "end": v(-50.25, 20.6) * mm});
            skLineSegment(sketch, "E371", {"start": v(-50.25, 20.6) * mm, "end": v(-50.29, 20.43) * mm});
            skLineSegment(sketch, "E372", {"start": v(-50.29, 20.43) * mm, "end": v(-50.37, 20.17) * mm});
            skLineSegment(sketch, "E373", {"start": v(-50.37, 20.17) * mm, "end": v(-50.5, 19.83) * mm});
            skLineSegment(sketch, "E374", {"start": v(-50.5, 19.83) * mm, "end": v(-50.83, 18.99) * mm});
            skLineSegment(sketch, "E375", {"start": v(-50.83, 18.99) * mm, "end": v(-51.26, 17.98) * mm});
            skLineSegment(sketch, "E376", {"start": v(-51.26, 17.98) * mm, "end": v(-52.4, 15.4) * mm});
            skLineSegment(sketch, "E377", {"start": v(-52.4, 15.4) * mm, "end": v(-47.66, 19.45) * mm});
            skLineSegment(sketch, "E378", {"start": v(-47.66, 19.45) * mm, "end": v(-44.48, 17.8) * mm});
            skLineSegment(sketch, "E379", {"start": v(-44.48, 17.8) * mm, "end": v(-44.03, 21.93) * mm});
            skLineSegment(sketch, "E380", {"start": v(-44.43, 24.98) * mm, "end": v(-45.16, 24.98) * mm});
            skLineSegment(sketch, "E381", {"start": v(-45.16, 24.98) * mm, "end": v(-45.16, 29.36) * mm});
            skLineSegment(sketch, "E382", {"start": v(136.74, 32.76) * mm, "end": v(173.08, 58.15) * mm});
            skLineSegment(sketch, "E383", {"start": v(173.08, 58.15) * mm, "end": v(173.87, 59.33) * mm});
            skLineSegment(sketch, "E384", {"start": v(173.87, 59.33) * mm, "end": v(170.44, 68.58) * mm});
            skLineSegment(sketch, "E385", {"start": v(170.44, 68.58) * mm, "end": v(167.62, 68.55) * mm});
            skLineSegment(sketch, "E386", {"start": v(167.62, 68.55) * mm, "end": v(124.74, 64.23) * mm});
            skLineSegment(sketch, "E387", {"start": v(124.74, 64.23) * mm, "end": v(124.23, 63.72) * mm});
            skLineSegment(sketch, "E388", {"start": v(124.23, 63.72) * mm, "end": v(127.47, 55.21) * mm});
            skLineSegment(sketch, "E389", {"start": v(127.47, 55.21) * mm, "end": v(127.72, 54.97) * mm});
            skLineSegment(sketch, "E390", {"start": v(127.72, 54.97) * mm, "end": v(137.05, 56.17) * mm});
            skLineSegment(sketch, "E391", {"start": v(137.05, 56.17) * mm, "end": v(137.4, 55.18) * mm});
            skLineSegment(sketch, "E392", {"start": v(137.4, 55.18) * mm, "end": v(138.16, 53.08) * mm});
            skLineSegment(sketch, "E393", {"start": v(140.15, 47.63) * mm, "end": v(140.13, 46.55) * mm});
            skLineSegment(sketch, "E394", {"start": v(140.13, 46.55) * mm, "end": v(133.24, 42.07) * mm});
            skLineSegment(sketch, "E395", {"start": v(133.24, 42.07) * mm, "end": v(132.8, 40.94) * mm});
            skLineSegment(sketch, "E396", {"start": v(132.8, 40.94) * mm, "end": v(135.83, 32.7) * mm});
            skLineSegment(sketch, "E397", {"start": v(135.83, 32.7) * mm, "end": v(136.74, 32.76) * mm});
            skLineSegment(sketch, "E398", {"start": v(-135.7, 34.06) * mm, "end": v(-132.36, 42.84) * mm});
            skLineSegment(sketch, "E399", {"start": v(-132.36, 42.84) * mm, "end": v(-132.6, 43.05) * mm});
            skLineSegment(sketch, "E400", {"start": v(-132.6, 43.05) * mm, "end": v(-157.57, 53.21) * mm});
            skLineSegment(sketch, "E401", {"start": v(-157.57, 53.21) * mm, "end": v(-158.28, 53.9) * mm});
            skLineSegment(sketch, "E402", {"start": v(-158.28, 53.9) * mm, "end": v(-142.3, 55.08) * mm});
            skLineSegment(sketch, "E403", {"start": v(-142.3, 55.08) * mm, "end": v(-139.4, 55.67) * mm});
            skLineSegment(sketch, "E404", {"start": v(-139.4, 55.67) * mm, "end": v(-139.16, 57.45) * mm});
            skLineSegment(sketch, "E405", {"start": v(-139.16, 57.45) * mm, "end": v(-150.6, 70.93) * mm});
            skLineSegment(sketch, "E406", {"start": v(-150.6, 70.93) * mm, "end": v(-150.1, 71.44) * mm});
            skLineSegment(sketch, "E407", {"start": v(-150.1, 71.44) * mm, "end": v(-125.12, 61.32) * mm});
            skLineSegment(sketch, "E408", {"start": v(-125.12, 61.32) * mm, "end": v(-124.79, 61.32) * mm});
            skLineSegment(sketch, "E409", {"start": v(-124.79, 61.32) * mm, "end": v(-121.3, 69.93) * mm});
            skLineSegment(sketch, "E410", {"start": v(-121.3, 69.93) * mm, "end": v(-121.7, 70.23) * mm});
            skLineSegment(sketch, "E411", {"start": v(-121.7, 70.23) * mm, "end": v(-161.66, 86.39) * mm});
            skLineSegment(sketch, "E412", {"start": v(-161.66, 86.39) * mm, "end": v(-162.69, 86.8) * mm});
            skLineSegment(sketch, "E413", {"start": v(-162.69, 86.8) * mm, "end": v(-166.08, 78.23) * mm});
            skLineSegment(sketch, "E414", {"start": v(-166.08, 78.23) * mm, "end": v(-153.17, 62.15) * mm});
            skLineSegment(sketch, "E415", {"start": v(-153.17, 62.15) * mm, "end": v(-153.48, 61.86) * mm});
            skLineSegment(sketch, "E416", {"start": v(-153.48, 61.86) * mm, "end": v(-173.76, 59.27) * mm});
            skLineSegment(sketch, "E417", {"start": v(-173.76, 59.27) * mm, "end": v(-177.23, 50.86) * mm});
            skLineSegment(sketch, "E418", {"start": v(-177.23, 50.86) * mm, "end": v(-176.65, 50.51) * mm});
            skLineSegment(sketch, "E419", {"start": v(-176.65, 50.51) * mm, "end": v(-136.02, 34.06) * mm});
            skLineSegment(sketch, "E420", {"start": v(-136.02, 34.06) * mm, "end": v(-135.7, 34.06) * mm});
            skLineSegment(sketch, "E421", {"start": v(144.36, 57.23) * mm, "end": v(144.96, 55.55) * mm});
            skLineSegment(sketch, "E422", {"start": v(146.63, 50.87) * mm, "end": v(147.13, 50.87) * mm});
            skLineSegment(sketch, "E423", {"start": v(147.13, 50.87) * mm, "end": v(160.55, 59.27) * mm});
            skLineSegment(sketch, "E424", {"start": v(160.55, 59.27) * mm, "end": v(159.81, 59.53) * mm});
            skLineSegment(sketch, "E425", {"start": v(159.81, 59.53) * mm, "end": v(144.66, 57.23) * mm});
            skLineSegment(sketch, "E426", {"start": v(144.66, 57.23) * mm, "end": v(144.36, 57.23) * mm});
            skLineSegment(sketch, "E427", {"start": v(114.94, 78.65) * mm, "end": v(140.04, 97.42) * mm});
            skLineSegment(sketch, "E428", {"start": v(140.04, 97.42) * mm, "end": v(144.15, 100.37) * mm});
            skLineSegment(sketch, "E429", {"start": v(144.15, 100.37) * mm, "end": v(150.16, 92.16) * mm});
            skLineSegment(sketch, "E430", {"start": v(156.43, 96.97) * mm, "end": v(138.24, 121.28) * mm});
            skLineSegment(sketch, "E431", {"start": v(138.24, 121.28) * mm, "end": v(132.2, 117.03) * mm});
            skLineSegment(sketch, "E432", {"start": v(132.2, 117.03) * mm, "end": v(131.91, 116.82) * mm});
            skLineSegment(sketch, "E433", {"start": v(131.91, 116.82) * mm, "end": v(137.87, 108.78) * mm});
            skLineSegment(sketch, "E434", {"start": v(137.87, 108.78) * mm, "end": v(137.84, 108.32) * mm});
            skLineSegment(sketch, "E435", {"start": v(137.84, 108.32) * mm, "end": v(108.4, 86.6) * mm});
            skLineSegment(sketch, "E436", {"start": v(108.4, 86.6) * mm, "end": v(108.97, 85.61) * mm});
            skLineSegment(sketch, "E437", {"start": v(108.97, 85.61) * mm, "end": v(114.3, 78.57) * mm});
            skLineSegment(sketch, "E438", {"start": v(114.3, 78.57) * mm, "end": v(114.94, 78.65) * mm});
            skLineSegment(sketch, "E439", {"start": v(-110.73, 83.57) * mm, "end": v(-104.66, 91.3) * mm});
            skLineSegment(sketch, "E440", {"start": v(-104.66, 91.3) * mm, "end": v(-104.66, 91.75) * mm});
            skLineSegment(sketch, "E441", {"start": v(-104.66, 91.75) * mm, "end": v(-138.83, 119.9) * mm});
            skLineSegment(sketch, "E442", {"start": v(-138.83, 119.9) * mm, "end": v(-144.85, 112.53) * mm});
            skLineSegment(sketch, "E443", {"start": v(-144.85, 112.53) * mm, "end": v(-145.13, 111.8) * mm});
            skLineSegment(sketch, "E444", {"start": v(-145.13, 111.8) * mm, "end": v(-112.6, 85.24) * mm});
            skLineSegment(sketch, "E445", {"start": v(-112.6, 85.24) * mm, "end": v(-110.73, 83.57) * mm});
            skLineSegment(sketch, "E446", {"start": v(-91.26, 105.4) * mm, "end": v(-83.79, 110.52) * mm});
            skLineSegment(sketch, "E447", {"start": v(-83.79, 110.52) * mm, "end": v(-84.53, 111.5) * mm});
            skLineSegment(sketch, "E448", {"start": v(-84.53, 111.5) * mm, "end": v(-97.93, 130.87) * mm});
            skLineSegment(sketch, "E449", {"start": v(-97.93, 130.87) * mm, "end": v(-97.46, 131.34) * mm});
            skLineSegment(sketch, "E450", {"start": v(-97.46, 131.34) * mm, "end": v(-73.94, 118.09) * mm});
            skLineSegment(sketch, "E451", {"start": v(-73.94, 118.09) * mm, "end": v(-72.9, 118.09) * mm});
            skLineSegment(sketch, "E452", {"start": v(-72.9, 118.09) * mm, "end": v(-66.1, 122.86) * mm});
            skLineSegment(sketch, "E453", {"start": v(-66.1, 122.86) * mm, "end": v(-67.19, 124.46) * mm});
            skLineSegment(sketch, "E454", {"start": v(-67.19, 124.46) * mm, "end": v(-91.26, 159.39) * mm});
            skLineSegment(sketch, "E455", {"start": v(-91.26, 159.39) * mm, "end": v(-91.97, 159.42) * mm});
            skLineSegment(sketch, "E456", {"start": v(-91.97, 159.42) * mm, "end": v(-99.2, 154.35) * mm});
            skLineSegment(sketch, "E457", {"start": v(-99.2, 154.35) * mm, "end": v(-99.2, 153.74) * mm});
            skLineSegment(sketch, "E458", {"start": v(-99.2, 153.74) * mm, "end": v(-85.69, 134.21) * mm});
            skLineSegment(sketch, "E459", {"start": v(-85.69, 134.21) * mm, "end": v(-85.98, 133.9) * mm});
            skLineSegment(sketch, "E460", {"start": v(-85.98, 133.9) * mm, "end": v(-108.97, 146.84) * mm});
            skLineSegment(sketch, "E461", {"start": v(-108.97, 146.84) * mm, "end": v(-109.93, 146.85) * mm});
            skLineSegment(sketch, "E462", {"start": v(-109.93, 146.85) * mm, "end": v(-116.92, 142.13) * mm});
            skLineSegment(sketch, "E463", {"start": v(-116.92, 142.13) * mm, "end": v(-116.92, 141.39) * mm});
            skLineSegment(sketch, "E464", {"start": v(-116.92, 141.39) * mm, "end": v(-92.17, 105.66) * mm});
            skLineSegment(sketch, "E465", {"start": v(-92.17, 105.66) * mm, "end": v(-91.26, 105.4) * mm});
            skLineSegment(sketch, "E466", {"start": v(115.7, 142.1) * mm, "end": v(114.58, 143.3) * mm});
            skLineSegment(sketch, "E467", {"start": v(86.25, 108.14) * mm, "end": v(89.5, 106.58) * mm});
            skLineSegment(sketch, "E468", {"start": v(108.95, 135.85) * mm, "end": v(108.77, 136.1) * mm});
            skLineSegment(sketch, "E469", {"start": v(105.13, 139.76) * mm, "end": v(104.7, 140.08) * mm});
            skLineSegment(sketch, "E470", {"start": v(87.84, 118.29) * mm, "end": v(87.84, 118.29) * mm});
            skLineSegment(sketch, "E471", {"start": v(53.17, 128.62) * mm, "end": v(55.34, 129.06) * mm});
            skLineSegment(sketch, "E472", {"start": v(55.34, 129.06) * mm, "end": v(55.9, 129.2) * mm});
            skLineSegment(sketch, "E473", {"start": v(55.9, 129.2) * mm, "end": v(56.32, 129.31) * mm});
            skLineSegment(sketch, "E474", {"start": v(56.32, 129.31) * mm, "end": v(56.73, 129.44) * mm});
            skLineSegment(sketch, "E475", {"start": v(56.73, 129.44) * mm, "end": v(57.12, 129.57) * mm});
            skLineSegment(sketch, "E476", {"start": v(57.12, 129.57) * mm, "end": v(57.48, 129.7) * mm});
            skLineSegment(sketch, "E477", {"start": v(57.48, 129.7) * mm, "end": v(57.78, 129.82) * mm});
            skLineSegment(sketch, "E478", {"start": v(57.78, 129.82) * mm, "end": v(58.03, 129.94) * mm});
            skLineSegment(sketch, "E479", {"start": v(58.03, 129.94) * mm, "end": v(58.27, 130.07) * mm});
            skLineSegment(sketch, "E480", {"start": v(58.27, 130.07) * mm, "end": v(58.55, 130.24) * mm});
            skLineSegment(sketch, "E481", {"start": v(58.55, 130.24) * mm, "end": v(59.2, 130.66) * mm});
            skLineSegment(sketch, "E482", {"start": v(59.2, 130.66) * mm, "end": v(59.89, 131.13) * mm});
            skLineSegment(sketch, "E483", {"start": v(59.89, 131.13) * mm, "end": v(60.54, 131.6) * mm});
            skLineSegment(sketch, "E484", {"start": v(60.54, 131.6) * mm, "end": v(62, 132.7) * mm});
            skLineSegment(sketch, "E485", {"start": v(62, 132.7) * mm, "end": v(64.75, 138.22) * mm});
            skLineSegment(sketch, "E486", {"start": v(64.75, 138.22) * mm, "end": v(64.74, 144.2) * mm});
            skLineSegment(sketch, "E487", {"start": v(64.74, 144.2) * mm, "end": v(63.44, 148.5) * mm});
            skLineSegment(sketch, "E488", {"start": v(63.44, 148.5) * mm, "end": v(58.74, 159.11) * mm});
            skLineSegment(sketch, "E489", {"start": v(63.21, 164.42) * mm, "end": v(67.3, 161.82) * mm});
            skLineSegment(sketch, "E490", {"start": v(67.3, 161.82) * mm, "end": v(68.74, 160.08) * mm});
            skLineSegment(sketch, "E491", {"start": v(68.74, 160.08) * mm, "end": v(69.03, 159.73) * mm});
            skLineSegment(sketch, "E492", {"start": v(69.03, 159.73) * mm, "end": v(69.32, 159.42) * mm});
            skLineSegment(sketch, "E493", {"start": v(69.32, 159.42) * mm, "end": v(69.58, 159.14) * mm});
            skLineSegment(sketch, "E494", {"start": v(69.58, 159.14) * mm, "end": v(69.82, 158.9) * mm});
            skLineSegment(sketch, "E495", {"start": v(69.82, 158.9) * mm, "end": v(70.03, 158.73) * mm});
            skLineSegment(sketch, "E496", {"start": v(70.03, 158.73) * mm, "end": v(70.2, 158.6) * mm});
            skLineSegment(sketch, "E497", {"start": v(70.2, 158.6) * mm, "end": v(70.26, 158.56) * mm});
            skLineSegment(sketch, "E498", {"start": v(70.26, 158.56) * mm, "end": v(70.32, 158.54) * mm});
            skLineSegment(sketch, "E499", {"start": v(70.32, 158.54) * mm, "end": v(70.36, 158.54) * mm});
            skLineSegment(sketch, "E500", {"start": v(70.36, 158.54) * mm, "end": v(70.4, 158.55) * mm});
            skLineSegment(sketch, "E501", {"start": v(70.4, 158.55) * mm, "end": v(70.6, 158.76) * mm});
            skLineSegment(sketch, "E502", {"start": v(70.6, 158.76) * mm, "end": v(73.33, 166.16) * mm});
            skLineSegment(sketch, "E503", {"start": v(73.33, 166.16) * mm, "end": v(69.07, 170.13) * mm});
            skLineSegment(sketch, "E504", {"start": v(69.07, 170.13) * mm, "end": v(67, 171.13) * mm});
            skLineSegment(sketch, "E505", {"start": v(67, 171.13) * mm, "end": v(66.53, 171.34) * mm});
            skLineSegment(sketch, "E506", {"start": v(66.53, 171.34) * mm, "end": v(66, 171.56) * mm});
            skLineSegment(sketch, "E507", {"start": v(66, 171.56) * mm, "end": v(65.41, 171.78) * mm});
            skLineSegment(sketch, "E508", {"start": v(65.41, 171.78) * mm, "end": v(64.8, 171.99) * mm});
            skLineSegment(sketch, "E509", {"start": v(64.8, 171.99) * mm, "end": v(64.17, 172.18) * mm});
            skLineSegment(sketch, "E510", {"start": v(64.17, 172.18) * mm, "end": v(63.56, 172.36) * mm});
            skLineSegment(sketch, "E511", {"start": v(63.56, 172.36) * mm, "end": v(62.96, 172.51) * mm});
            skLineSegment(sketch, "E512", {"start": v(62.96, 172.51) * mm, "end": v(62.42, 172.64) * mm});
            skLineSegment(sketch, "E513", {"start": v(62.42, 172.64) * mm, "end": v(59.9, 173.14) * mm});
            skLineSegment(sketch, "E514", {"start": v(48.28, 159.9) * mm, "end": v(48.86, 157.73) * mm});
            skLineSegment(sketch, "E515", {"start": v(48.86, 157.73) * mm, "end": v(49.03, 157.2) * mm});
            skLineSegment(sketch, "E516", {"start": v(49.03, 157.2) * mm, "end": v(49.27, 156.5) * mm});
            skLineSegment(sketch, "E517", {"start": v(49.27, 156.5) * mm, "end": v(49.57, 155.68) * mm});
            skLineSegment(sketch, "E518", {"start": v(49.57, 155.68) * mm, "end": v(49.93, 154.76) * mm});
            skLineSegment(sketch, "E519", {"start": v(49.93, 154.76) * mm, "end": v(50.33, 153.77) * mm});
            skLineSegment(sketch, "E520", {"start": v(50.33, 153.77) * mm, "end": v(50.76, 152.74) * mm});
            skLineSegment(sketch, "E521", {"start": v(50.76, 152.74) * mm, "end": v(51.2, 151.7) * mm});
            skLineSegment(sketch, "E522", {"start": v(51.2, 151.7) * mm, "end": v(51.66, 150.67) * mm});
            skLineSegment(sketch, "E523", {"start": v(51.66, 150.67) * mm, "end": v(52.12, 149.64) * mm});
            skLineSegment(sketch, "E524", {"start": v(52.12, 149.64) * mm, "end": v(52.56, 148.6) * mm});
            skLineSegment(sketch, "E525", {"start": v(52.56, 148.6) * mm, "end": v(52.98, 147.56) * mm});
            skLineSegment(sketch, "E526", {"start": v(52.98, 147.56) * mm, "end": v(53.37, 146.57) * mm});
            skLineSegment(sketch, "E527", {"start": v(53.37, 146.57) * mm, "end": v(53.72, 145.65) * mm});
            skLineSegment(sketch, "E528", {"start": v(53.72, 145.65) * mm, "end": v(54, 144.82) * mm});
            skLineSegment(sketch, "E529", {"start": v(54, 144.82) * mm, "end": v(54.23, 144.13) * mm});
            skLineSegment(sketch, "E530", {"start": v(54.23, 144.13) * mm, "end": v(54.31, 143.84) * mm});
            skLineSegment(sketch, "E531", {"start": v(54.31, 143.84) * mm, "end": v(54.38, 143.59) * mm});
            skLineSegment(sketch, "E532", {"start": v(54.38, 143.59) * mm, "end": v(54.88, 141.4) * mm});
            skLineSegment(sketch, "E533", {"start": v(46.81, 139.23) * mm, "end": v(42.5, 144.89) * mm});
            skLineSegment(sketch, "E534", {"start": v(42.5, 144.89) * mm, "end": v(42.04, 144.89) * mm});
            skLineSegment(sketch, "E535", {"start": v(42.04, 144.89) * mm, "end": v(38.86, 137.4) * mm});
            skLineSegment(sketch, "E536", {"start": v(38.86, 137.4) * mm, "end": v(38.86, 136.4) * mm});
            skLineSegment(sketch, "E537", {"start": v(38.86, 136.4) * mm, "end": v(44.29, 131.22) * mm});
            skLineSegment(sketch, "E538", {"start": v(44.29, 131.22) * mm, "end": v(49.08, 129.08) * mm});
            skLineSegment(sketch, "E539", {"start": v(49.08, 129.08) * mm, "end": v(53.17, 128.62) * mm});
            skLineSegment(sketch, "E540", {"start": v(-45.08, 131.43) * mm, "end": v(-41.6, 132.4) * mm});
            skLineSegment(sketch, "E541", {"start": v(-41.6, 132.4) * mm, "end": v(-41.1, 132.89) * mm});
            skLineSegment(sketch, "E542", {"start": v(-41.1, 132.89) * mm, "end": v(-47.43, 156.92) * mm});
            skLineSegment(sketch, "E543", {"start": v(-47.43, 156.92) * mm, "end": v(-47.2, 157.6) * mm});
            skLineSegment(sketch, "E544", {"start": v(-47.2, 157.6) * mm, "end": v(-29.67, 136.79) * mm});
            skLineSegment(sketch, "E545", {"start": v(-29.67, 136.79) * mm, "end": v(-28.55, 135.86) * mm});
            skLineSegment(sketch, "E546", {"start": v(-28.55, 135.86) * mm, "end": v(-20.86, 137.74) * mm});
            skLineSegment(sketch, "E547", {"start": v(-20.86, 137.74) * mm, "end": v(-20.13, 138.4) * mm});
            skLineSegment(sketch, "E548", {"start": v(-20.13, 138.4) * mm, "end": v(-31.24, 181) * mm});
            skLineSegment(sketch, "E549", {"start": v(-31.24, 181) * mm, "end": v(-31.45, 181.29) * mm});
            skLineSegment(sketch, "E550", {"start": v(-31.45, 181.29) * mm, "end": v(-40.34, 178.92) * mm});
            skLineSegment(sketch, "E551", {"start": v(-40.34, 178.92) * mm, "end": v(-40.65, 178.61) * mm});
            skLineSegment(sketch, "E552", {"start": v(-40.65, 178.61) * mm, "end": v(-34.67, 156.01) * mm});
            skLineSegment(sketch, "E553", {"start": v(-34.67, 156.01) * mm, "end": v(-34.49, 154.52) * mm});
            skLineSegment(sketch, "E554", {"start": v(-34.49, 154.52) * mm, "end": v(-52.2, 175.4) * mm});
            skLineSegment(sketch, "E555", {"start": v(-52.2, 175.4) * mm, "end": v(-52.8, 175.77) * mm});
            skLineSegment(sketch, "E556", {"start": v(-52.8, 175.77) * mm, "end": v(-61.17, 173.53) * mm});
            skLineSegment(sketch, "E557", {"start": v(-61.17, 173.53) * mm, "end": v(-61.62, 173.08) * mm});
            skLineSegment(sketch, "E558", {"start": v(-61.62, 173.08) * mm, "end": v(-50.61, 130.9) * mm});
            skLineSegment(sketch, "E559", {"start": v(-50.61, 130.9) * mm, "end": v(-50.61, 130.63) * mm});
            skLineSegment(sketch, "E560", {"start": v(-50.61, 130.63) * mm, "end": v(-50.6, 130.59) * mm});
            skLineSegment(sketch, "E561", {"start": v(-50.6, 130.59) * mm, "end": v(-50.59, 130.55) * mm});
            skLineSegment(sketch, "E562", {"start": v(-50.59, 130.55) * mm, "end": v(-50.56, 130.51) * mm});
            skLineSegment(sketch, "E563", {"start": v(-50.56, 130.51) * mm, "end": v(-50.52, 130.48) * mm});
            skLineSegment(sketch, "E564", {"start": v(-50.52, 130.48) * mm, "end": v(-50.41, 130.44) * mm});
            skLineSegment(sketch, "E565", {"start": v(-50.41, 130.44) * mm, "end": v(-50.26, 130.41) * mm});
            skLineSegment(sketch, "E566", {"start": v(-50.26, 130.41) * mm, "end": v(-50.06, 130.4) * mm});
            skLineSegment(sketch, "E567", {"start": v(-50.06, 130.4) * mm, "end": v(-49.81, 130.4) * mm});
            skLineSegment(sketch, "E568", {"start": v(-49.81, 130.4) * mm, "end": v(-49.53, 130.43) * mm});
            skLineSegment(sketch, "E569", {"start": v(-49.53, 130.43) * mm, "end": v(-49.2, 130.48) * mm});
            skLineSegment(sketch, "E570", {"start": v(-49.2, 130.48) * mm, "end": v(-48.83, 130.53) * mm});
            skLineSegment(sketch, "E571", {"start": v(-48.83, 130.53) * mm, "end": v(-48.42, 130.61) * mm});
            skLineSegment(sketch, "E572", {"start": v(-48.42, 130.61) * mm, "end": v(-47.47, 130.82) * mm});
            skLineSegment(sketch, "E573", {"start": v(-47.47, 130.82) * mm, "end": v(-46.36, 131.09) * mm});
            skLineSegment(sketch, "E574", {"start": v(-46.36, 131.09) * mm, "end": v(-45.08, 131.43) * mm});
            skLineSegment(sketch, "E575", {"start": v(24.4, 144.44) * mm, "end": v(7.78, 145.73) * mm});
            skLineSegment(sketch, "E576", {"start": v(7.78, 145.73) * mm, "end": v(8.54, 156.92) * mm});
            skLineSegment(sketch, "E577", {"start": v(8.54, 156.92) * mm, "end": v(8.8, 157.22) * mm});
            skLineSegment(sketch, "E578", {"start": v(8.8, 157.22) * mm, "end": v(23.02, 156.12) * mm});
            skLineSegment(sketch, "E579", {"start": v(23.02, 156.12) * mm, "end": v(23.38, 156.5) * mm});
            skLineSegment(sketch, "E580", {"start": v(23.38, 156.5) * mm, "end": v(24, 163.83) * mm});
            skLineSegment(sketch, "E581", {"start": v(9.23, 165) * mm, "end": v(9.88, 175.09) * mm});
            skLineSegment(sketch, "E582", {"start": v(9.88, 175.09) * mm, "end": v(10.14, 175.36) * mm});
            skLineSegment(sketch, "E583", {"start": v(10.14, 175.36) * mm, "end": v(25.6, 174.16) * mm});
            skLineSegment(sketch, "E584", {"start": v(26.15, 181.96) * mm, "end": v(0.72, 183.93) * mm});
            skLineSegment(sketch, "E585", {"start": v(0.72, 183.93) * mm, "end": v(0.28, 183.21) * mm});
            skLineSegment(sketch, "E586", {"start": v(0.28, 183.21) * mm, "end": v(-2.62, 139.85) * mm});
            skLineSegment(sketch, "E587", {"start": v(-2.62, 139.85) * mm, "end": v(23.96, 137.79) * mm});
            skLineSegment(sketch, "E588", {"start": v(106.57, 38.1) * mm, "end": v(113.35, 40.34) * mm});
            skLineSegment(sketch, "E589", {"start": v(115.32, 34.3) * mm, "end": v(108.8, 32.15) * mm});
            skLineSegment(sketch, "E590", {"start": v(138.16, 53.08) * mm, "end": v(144.96, 55.55) * mm});
            skLineSegment(sketch, "E591", {"start": v(139.35, 49.91) * mm, "end": v(146.1, 52.37) * mm});
            skLineSegment(sketch, "E592.trimOffspring", {"start": v(146.1, 52.37) * mm, "end": v(146.63, 50.87) * mm});
            skLineSegment(sketch, "E593", {"start": v(-112.72, -8.63) * mm, "end": v(-119.82, -10.85) * mm});
            skLineSegment(sketch, "E594", {"start": v(-109.87, -14.3) * mm, "end": v(-119.08, -17.16) * mm});
            skPoint(sketch, "E595.orphan", {"position": v(-117.87, -16.78) * mm});
            skPoint(sketch, "E596.end.orphan", {"position": v(-117.87, -16.64) * mm});
            skPoint(sketch, "E597.end.orphan", {"position": v(-109.96, -14.32) * mm});
            skLineSegment(sketch, "E598", {"start": v(110.75, 146.73) * mm, "end": v(105.13, 139.76) * mm});
            skLineSegment(sketch, "E599.trimOffspring", {"start": v(92.09, 115.38) * mm, "end": v(86.25, 108.14) * mm});
            skLineSegment(sketch, "E600.trimOffspring", {"start": v(87.84, 118.29) * mm, "end": v(82.2, 111.3) * mm});
            skLineSegment(sketch, "E601", {"start": v(114.58, 143.3) * mm, "end": v(108.77, 136.1) * mm});
            skLineSegment(sketch, "E602", {"start": v(76.13, -168.01) * mm, "end": v(72.9, -161.22) * mm});
            skLineSegment(sketch, "E603", {"start": v(79.3, -166.47) * mm, "end": v(75.92, -159.35) * mm});
            skLineSegment(sketch, "E604.trimOffspring", {"start": v(63.6, -133.49) * mm, "end": v(60.2, -126.35) * mm});
            skLineSegment(sketch, "E605.trimOffspring", {"start": v(60.23, -134.6) * mm, "end": v(56.92, -127.66) * mm});
            skLineSegment(sketch, "E606", {"start": v(140.15, 47.63) * mm, "end": v(139.35, 49.91) * mm});
            skCircle(sketch, "E607", {"center": v(0, 0) * mm, "radius": 203.87 * mm});
            skArc(sketch, "E608", {"start": v(98.59, -124.67) * mm, "mid": v(142.27, -81.88) * mm, "end": v(164.67, -24.98) * mm});
            skArc(sketch, "E609", {"start": v(98.59, -124.67) * mm, "mid": v(137.93, -78.5) * mm, "end": v(157.06, -20.94) * mm});
            skArc(sketch, "E610", {"start": v(-119.08, -17.16) * mm, "mid": v(25.8, -117.51) * mm, "end": v(115.32, 34.3) * mm});
            skArc(sketch, "E611.trimOffspring", {"start": v(113.35, 40.34) * mm, "mid": v(-25.8, 117.51) * mm, "end": v(-119.82, -10.85) * mm});
            skArc(sketch, "E612", {"start": v(165.17, -8.63) * mm, "mid": v(161.52, 11.74) * mm, "end": v(155.62, 31.57) * mm});
            skArc(sketch, "E613", {"start": v(158.25, -8.6) * mm, "mid": v(157.88, 11.54) * mm, "end": v(155.62, 31.57) * mm});
            skArc(sketch, "E614", {"start": v(-76.46, 20.53) * mm, "mid": v(-96.08, 9.04) * mm, "end": v(-114.52, -4.25) * mm});
            skArc(sketch, "E615", {"start": v(-22.2, 50.5) * mm, "mid": v(-53.92, 40.43) * mm, "end": v(-83.9, 25.97) * mm});
            skArc(sketch, "E616", {"start": v(-164.15, -27.02) * mm, "mid": v(-142.13, -83.44) * mm, "end": v(-98.07, -125) * mm});
            skArc(sketch, "E617", {"start": v(-157, -20.94) * mm, "mid": v(-137.6, -78.67) * mm, "end": v(-98.06, -125.01) * mm});
            skArc(sketch, "E618", {"start": v(-155.85, 31.36) * mm, "mid": v(-158.12, 11.44) * mm, "end": v(-158.2, -8.6) * mm});
            skArc(sketch, "E619", {"start": v(-155.85, 31.36) * mm, "mid": v(-161.47, 11.6) * mm, "end": v(-165.07, -8.63) * mm});
            skArc(sketch, "E620", {"start": v(-26.41, 12.38) * mm, "mid": v(-57.25, 4.18) * mm, "end": v(-87.17, -6.94) * mm});
            skArc(sketch, "E621", {"start": v(-26.41, 12.38) * mm, "mid": v(-34.05, 14.77) * mm, "end": v(-42, 15.67) * mm});
            skArc(sketch, "E622", {"start": v(58.58, 32.34) * mm, "mid": v(7.84, 26.7) * mm, "end": v(-42, 15.67) * mm});
            skArc(sketch, "E623", {"start": v(8.2, 32.61) * mm, "mid": v(-18.33, 30.32) * mm, "end": v(-44.43, 24.98) * mm});
            skArc(sketch, "E624", {"start": v(8.2, 32.61) * mm, "mid": v(-18.15, 28.43) * mm, "end": v(-44.03, 21.93) * mm});
            skArc(sketch, "E625", {"start": v(94.31, 33.98) * mm, "mid": v(44.54, 44.44) * mm, "end": v(-6.31, 45.08) * mm});
            skArc(sketch, "E626", {"start": v(-48.28, 23.85) * mm, "mid": v(-59.67, 19.46) * mm, "end": v(-70.79, 14.43) * mm});
            skArc(sketch, "E627", {"start": v(58.58, 32.34) * mm, "mid": v(41.38, 36.98) * mm, "end": v(23.65, 38.66) * mm});
            skArc(sketch, "E628", {"start": v(22.39, 39.08) * mm, "mid": v(-20.72, 37.41) * mm, "end": v(-62.92, 28.48) * mm});
            skArc(sketch, "E629", {"start": v(97.18, 47.66) * mm, "mid": v(67.14, 51.9) * mm, "end": v(36.82, 52.7) * mm});
            skArc(sketch, "E630", {"start": v(27.06, 51.83) * mm, "mid": v(3.23, 62.97) * mm, "end": v(-14.7, 43.72) * mm});
            skArc(sketch, "E631", {"start": v(36.82, 52.7) * mm, "mid": v(6.58, 71.14) * mm, "end": v(-22.2, 50.5) * mm});
            skArc(sketch, "E632", {"start": v(-14.7, 43.72) * mm, "mid": v(-40.22, 37.94) * mm, "end": v(-64.64, 28.57) * mm});
            skArc(sketch, "E633", {"start": v(106.57, 38.1) * mm, "mid": v(98.82, 40.47) * mm, "end": v(90.99, 42.52) * mm});
            skArc(sketch, "E634", {"start": v(27.06, 51.83) * mm, "mid": v(10.3, 49.64) * mm, "end": v(-6.24, 46.2) * mm});
            skArc(sketch, "E635", {"start": v(-114.52, -4.25) * mm, "mid": v(-113.65, -6.46) * mm, "end": v(-112.72, -8.63) * mm});
            skPoint(sketch, "E636.orphan", {"position": v(-112.9, -8.7) * mm});
            skArc(sketch, "E637.trimOffspring", {"start": v(-109.87, -14.3) * mm, "mid": v(-108.36, -16.88) * mm, "end": v(-106.74, -19.41) * mm});
            skArc(sketch, "E638", {"start": v(-22.22, -25.6) * mm, "mid": v(-30.53, -26.58) * mm, "end": v(-38.74, -28.2) * mm});
            skArc(sketch, "E639", {"start": v(79.3, -166.47) * mm, "mid": v(85.32, -139) * mm, "end": v(60.2, -126.35) * mm});
            skArc(sketch, "E640", {"start": v(75.92, -159.35) * mm, "mid": v(76.61, -143.16) * mm, "end": v(63.6, -133.49) * mm});
            skArc(sketch, "E641", {"start": v(89.5, 106.58) * mm, "mid": v(112.18, 117.27) * mm, "end": v(115.7, 142.1) * mm});
            skArc(sketch, "E642", {"start": v(110.75, 146.73) * mm, "mid": v(84, 139.06) * mm, "end": v(82.2, 111.3) * mm});
            skLineSegment(sketch, "E643", {"start": v(156.43, 96.97) * mm, "end": v(150.16, 92.16) * mm});
            skArc(sketch, "E644", {"start": v(104.7, 140.08) * mm, "mid": v(92.56, 132.05) * mm, "end": v(87.84, 118.29) * mm});
            skArc(sketch, "E645", {"start": v(92.09, 115.38) * mm, "mid": v(103.6, 123.08) * mm, "end": v(108.95, 135.85) * mm});
            skArc(sketch, "E646", {"start": v(59.9, 173.14) * mm, "mid": v(51.03, 169.2) * mm, "end": v(48.28, 159.9) * mm});
            skArc(sketch, "E647", {"start": v(63.21, 164.42) * mm, "mid": v(59.32, 163.16) * mm, "end": v(58.74, 159.11) * mm});
            skArc(sketch, "E648", {"start": v(46.81, 139.23) * mm, "mid": v(51.34, 138.46) * mm, "end": v(54.88, 141.4) * mm});
            skArc(sketch, "E649", {"start": v(19.39, -74.33) * mm, "mid": v(-8.97, -59.6) * mm, "end": v(-40.85, -61.7) * mm});
            skArc(sketch, "E650", {"start": v(-57.28, -55.08) * mm, "mid": v(-49.2, -58.74) * mm, "end": v(-40.85, -61.7) * mm});
            skLineSegment(sketch, "E651", {"start": v(23.78, -9.76) * mm, "end": v(15.53, -23.39) * mm});
            skLineSegment(sketch, "E652", {"start": v(24.4, 144.44) * mm, "end": v(23.96, 137.79) * mm});
            skLineSegment(sketch, "E653", {"start": v(26.15, 181.96) * mm, "end": v(25.6, 174.16) * mm});
            skLineSegment(sketch, "E654", {"start": v(9.23, 165) * mm, "end": v(24, 163.83) * mm});
            skArc(sketch, "E655", {"start": v(-43.12, -44.24) * mm, "mid": v(-38.5, -43.5) * mm, "end": v(-34.35, -41.36) * mm});
            skArc(sketch, "E656", {"start": v(-32.44, -38.94) * mm, "mid": v(-32.6, -36.99) * mm, "end": v(-33.72, -35.39) * mm});
            skArc(sketch, "E657", {"start": v(-60.33, -47.18) * mm, "mid": v(-59.11, -48.2) * mm, "end": v(-57.79, -49.05) * mm});
            skArc(sketch, "E658", {"start": v(-59.53, -50.79) * mm, "mid": v(-58.55, -50.2) * mm, "end": v(-57.65, -49.5) * mm});
            skArc(sketch, "E659", {"start": v(-51.65, -34.33) * mm, "mid": v(-53.1, -33.16) * mm, "end": v(-54.73, -32.24) * mm});
            skArc(sketch, "E660", {"start": v(-56.42, -27.3) * mm, "mid": v(-57.83, -28.69) * mm, "end": v(-57.64, -30.65) * mm});
            skArc(sketch, "E661", {"start": v(-71.8, -33.86) * mm, "mid": v(-68.68, -34.73) * mm, "end": v(-65.51, -35.4) * mm});
            skArc(sketch, "E662", {"start": v(-95.75, -27.84) * mm, "mid": v(-89, -31.06) * mm, "end": v(-82.13, -34) * mm});
            skArc(sketch, "E663", {"start": v(-106.74, -19.41) * mm, "mid": v(-104.2, -22.87) * mm, "end": v(-100.7, -25.36) * mm});
            skLineSegment(sketch, "E664", {"start": v(-15.26, -10) * mm, "end": v(-9.6, -20.5) * mm});
            skLineSegment(sketch, "E665", {"start": v(-48.28, 23.85) * mm, "end": v(-45.16, 29.36) * mm});
            skLineSegment(sketch, "E666", {"start": v(-19.58, 9.3) * mm, "end": v(-26.44, -2.22) * mm});
            skSolve(sketch);
        }
        {
            var Q0;
            Q0 = qSketchRegion(id + "F0", true);
            extrude(context, id + "F1", {"entities" : qUnion([Q0]), "depth" : 25.4 * mm});
        }
    });
